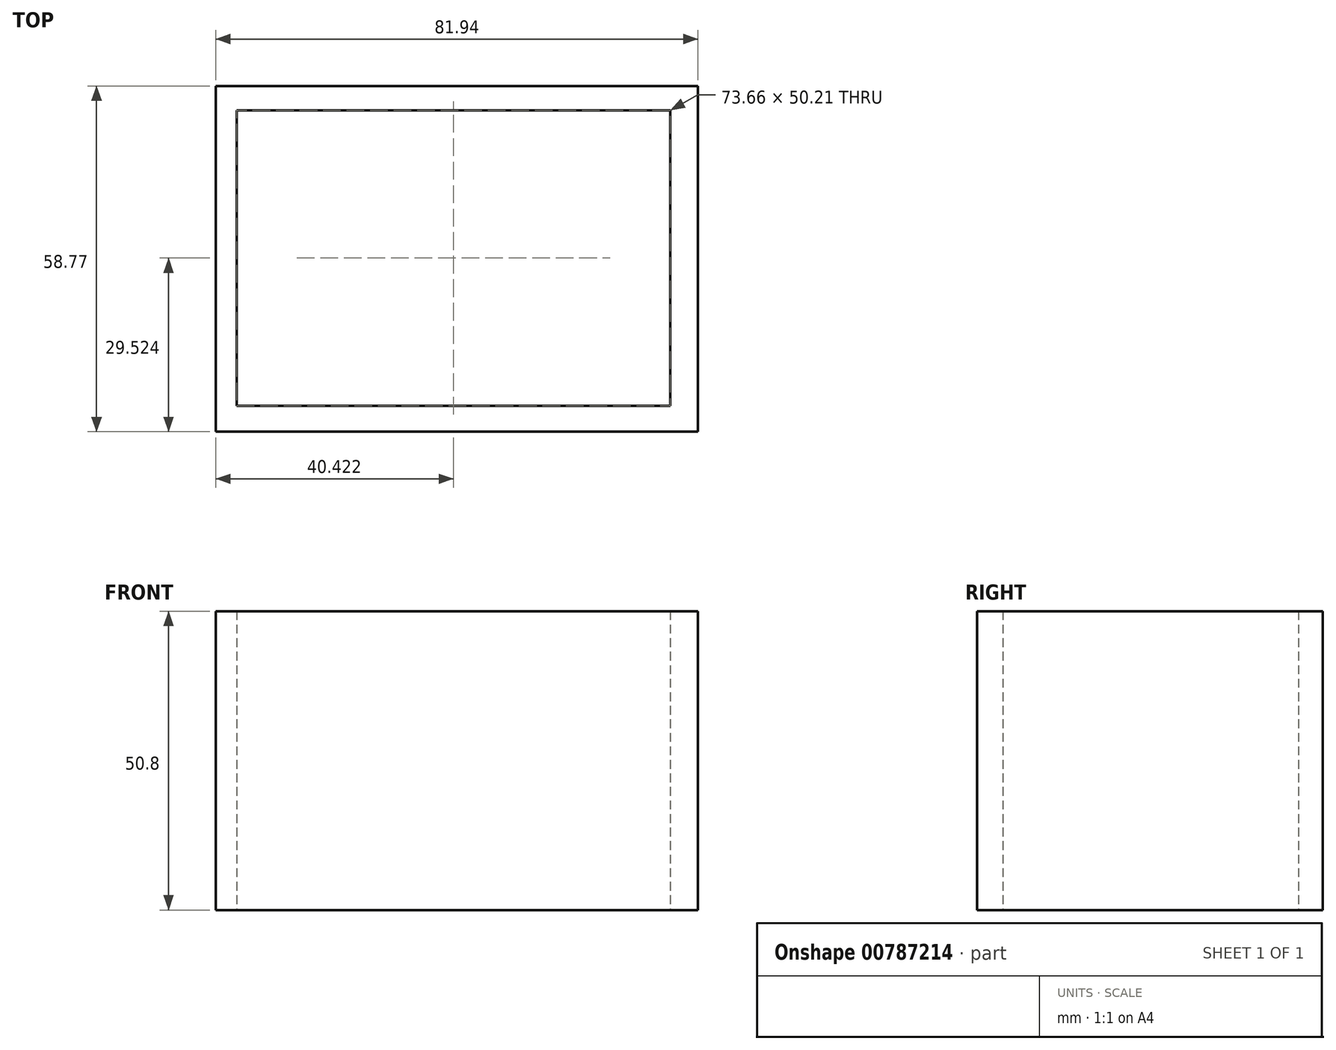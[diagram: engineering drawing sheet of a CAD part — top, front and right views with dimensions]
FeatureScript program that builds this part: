
annotation { "Feature Type Name" : "Feature", "Feature Type Description" : "" }
export const myFeature = defineFeature(function(context is Context, id is Id, definition is map)
    precondition{}
    {
        {
            var Q0;
            Q0=qCreatedBy(makeId("Top.planeOp"),FACE);
            var sketch = newSketch(context, id + "F0", { "sketchPlane" : qUnion([Q0])});
            skLineSegment(sketch, "E0.bottom", {"start": v(-32.97, 24.14) * mm, "end": v(40.7, 24.14) * mm});
            skLineSegment(sketch, "E0.top", {"start": v(-32.97, -26.07) * mm, "end": v(40.7, -26.07) * mm});
            skLineSegment(sketch, "E0.left", {"start": v(-32.97, 24.14) * mm, "end": v(-32.97, -26.07) * mm});
            skLineSegment(sketch, "E0.right", {"start": v(40.7, 24.14) * mm, "end": v(40.7, -26.07) * mm});
            skLineSegment(sketch, "E1.bottom", {"start": v(-36.56, 28.28) * mm, "end": v(45.38, 28.28) * mm});
            skLineSegment(sketch, "E1.top", {"start": v(-36.56, -30.49) * mm, "end": v(45.38, -30.49) * mm});
            skLineSegment(sketch, "E1.left", {"start": v(-36.56, 28.28) * mm, "end": v(-36.56, -30.49) * mm});
            skLineSegment(sketch, "E1.right", {"start": v(45.38, 28.28) * mm, "end": v(45.38, -30.49) * mm});
            skSolve(sketch);
        }
        {
            var Q0;
            Q0 = qSketchRegion(id + "F0", true);
            extrude(context, id + "F1", {"entities" : qUnion([Q0]), "depth" : 50.8 * mm, "offsetDistance" : 25.4 * mm});
        }
    });
